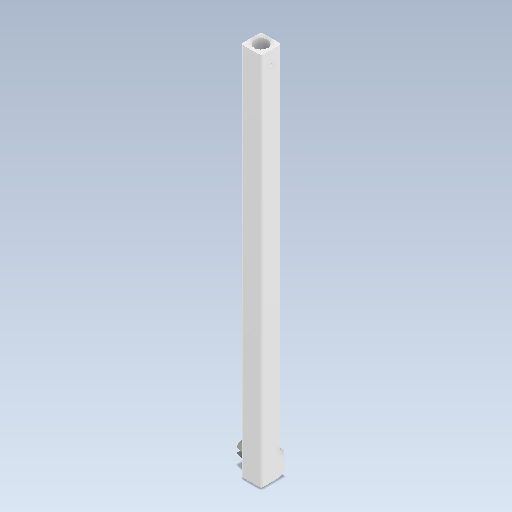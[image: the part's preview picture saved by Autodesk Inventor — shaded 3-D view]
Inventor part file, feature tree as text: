
AUTODESK INVENTOR PART (.ipt)
format: ipt  version: 2021 (Build 250183000, 183)  size: 303,616 bytes
history: native  units: mm
features: sketch x11, extrude x10, fillet x4, other x1, revolve x1, plane x1
ambient origin geometry x8: Origin, YZ Plane, XZ Plane, XY Plane, X Axis, Y Axis, Z Axis, Center Point
bodies: Body1 (feature_tree)
feature tree (28):
  other  "Sólido1"
  extrude  "Extrusión1"  Depth=5.0mm
  fillet  "Empalme1"  Radius=5.0mm
  extrude  "Extrusión2"  Depth=6.45mm
  extrude  "Extrusión3"  Depth=8.0mm
  fillet  "Empalme4"  Radius=1.0mm
  sketch  "Boceto11"  dims[d19=16.0mm d20=0.0mm d27=1.5mm]
  extrude  "Extrusión9"  Depth=8.0mm
  revolve  "Revolución1"  [1 undecoded]
  extrude  "Extrusión5"  TaperAngle=30.0deg  [1 undecoded]
  fillet  "Empalme2"  Radius=2.5mm
  plane  "Plano de trabajo2"
  extrude  "Extrusión6"  Depth=9.6mm
  extrude  "Extrusión7"  Depth=1.4mm
  extrude  "Extrusión8"  TaperAngle=0.0deg  [1 undecoded]
  fillet  "Empalme3"  Radius=1.5mm
  extrude  "Extrusión10"  Depth=3.0mm
  extrude  "Extrusión11"  Depth=0.5mm
  sketch  "Boceto1"  dims[d0=10.0mm d1=6.0mm d2=5.0mm]
  sketch  "Boceto2"  dims[d3=181.05mm d4=6.45mm]
  sketch  "Boceto3"  dims[d5=3.15mm d6=8.0mm d7=1.0mm]
  sketch  "Boceto6"  dims[d8=1.0mm d9=8.0mm]
  sketch  "Boceto7"  dims[d10=0.0mm d11=1.0mm]
  sketch  "Boceto8"  dims[d12=11.0mm d13=30.0deg d14=2.5mm]
  sketch  "Boceto9"  dims[d15=0.0mm d16=9.6mm]
  sketch  "Boceto10"  dims[d17=1.4mm d18=1.4mm]
  sketch  "Boceto13"  dims[d28=3.0mm d29=3.0mm]
  sketch  "Boceto14"  dims[d30=8.0mm d31=0.5mm d32=2.373201mm d33=90.0deg d34=1.5mm d35=3.0mm d36=5.0mm d37=1.0mm d38=7.0mm d39=2.0mm d40=7.0mm d41=0.0mm d45=1.5mm d46=1.0mm d49=2.0mm d50=32.0mm d51=32.0mm d52=34.0mm d53=0.0mm d55=2.0mm d56=5.5mm d57=44.2mm d58=0.0mm d59=6.0mm d60=2.0mm d61=0.0mm d62=1.0mm d63=1.0mm d66=6.0mm d67=181.05mm d68=6.45mm d69=5.45mm d70=2.3mm d72=0.0mm d73=0.0mm d77=177.05mm d78=0.0mm d79=0.0mm d80=0.0mm d81=32.0mm d82=32.0mm d83=181.05mm d84=0.0mm d85=6.0mm d86=137.85mm d87=4.0mm d88=1.0mm d89=0.0mm d90=0.0mm d44=0.5mm d47=0.872665mm]
note: 3 required parameter values undecoded (feature->parameter linkage not recoverable at this tier; creation-order binding heuristic only, values carry confidence <= 0.55)